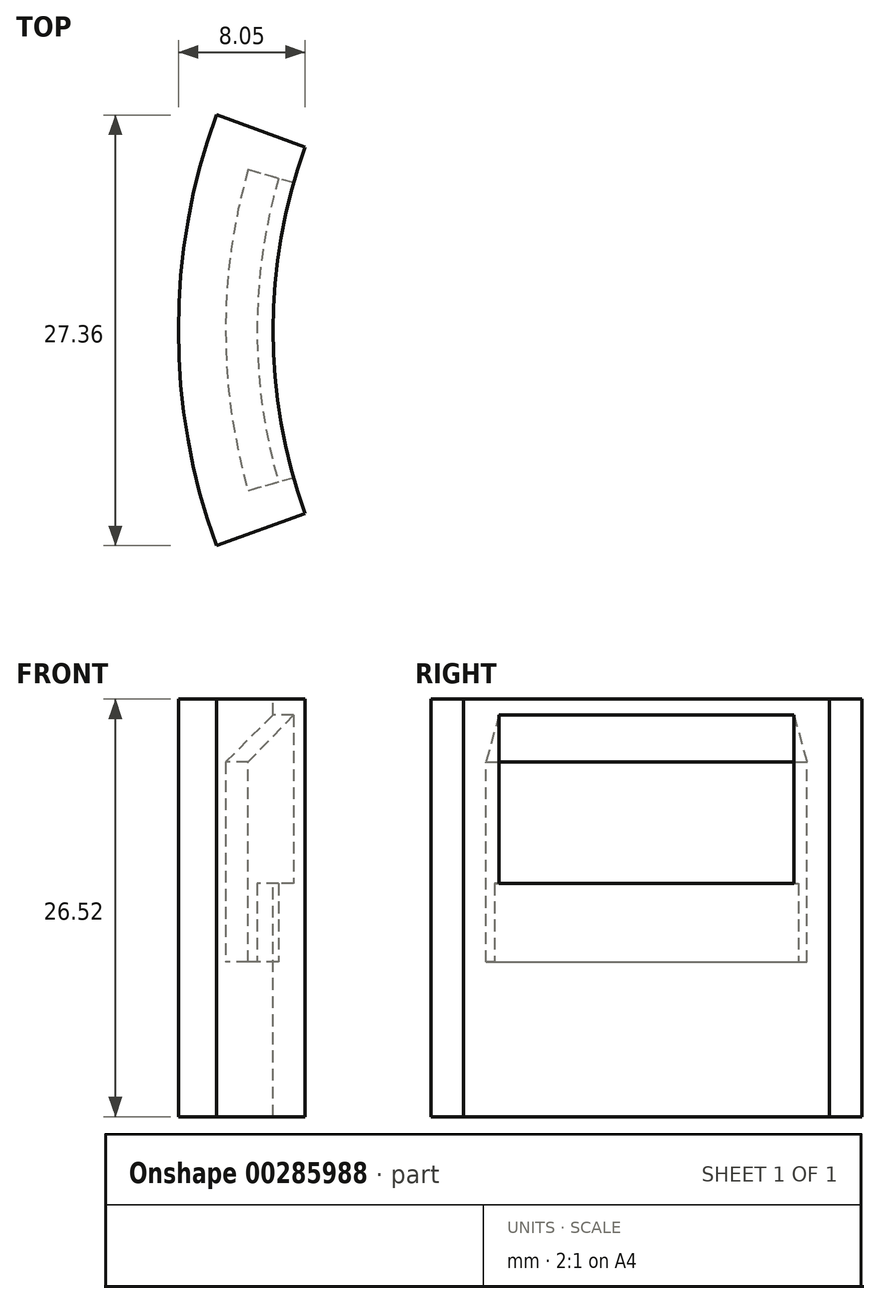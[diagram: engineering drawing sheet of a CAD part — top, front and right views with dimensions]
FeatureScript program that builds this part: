
annotation { "Feature Type Name" : "Feature", "Feature Type Description" : "" }
export const myFeature = defineFeature(function(context is Context, id is Id, definition is map)
    precondition{}
    {
        {
            var Q0;
            Q0=qCreatedBy(makeId("Front.planeOp"),FACE);
            var sketch = newSketch(context, id + "F0", { "sketchPlane" : qUnion([Q0])});
            skLineSegment(sketch, "E0", {"start": v(-34, 25.02) * mm, "end": v(0, 25.02) * mm, "construction": true});
            skLineSegment(sketch, "E1", {"start": v(-34, 25.02) * mm, "end": v(-34, 20.52) * mm});
            skLineSegment(sketch, "E2", {"start": v(-34, 20.52) * mm, "end": v(0, 20.52) * mm, "construction": true});
            skPoint(sketch, "E3", {"position": v(-34, 15.54) * mm});
            skLineSegment(sketch, "E4", {"start": v(-34, 20.52) * mm, "end": v(-37, 20.52) * mm, "construction": true});
            skLineSegment(sketch, "E5", {"start": v(-37, 20.52) * mm, "end": v(-37, 9.82) * mm});
            skPoint(sketch, "E6", {"position": v(-37, 15.17) * mm});
            skLineSegment(sketch, "E7", {"start": v(-37, 26.52) * mm, "end": v(-34, 26.52) * mm, "construction": true});
            skLineSegment(sketch, "E8", {"start": v(-34, 26.52) * mm, "end": v(-34, 25.02) * mm});
            skLineSegment(sketch, "E9", {"start": v(-34, 15.54) * mm, "end": v(-35, 15.54) * mm, "construction": true});
            skLineSegment(sketch, "E10", {"start": v(-35, 13.82) * mm, "end": v(-35, 15.54) * mm, "construction": true});
            skLineSegment(sketch, "E11", {"start": v(-34, 14.82) * mm, "end": v(-35, 14.82) * mm});
            skLineSegment(sketch, "E12", {"start": v(-35, 13.82) * mm, "end": v(-35, 14.82) * mm});
            skLineSegment(sketch, "E13", {"start": v(-35, 13.82) * mm, "end": v(-35, 9.82) * mm});
            skLineSegment(sketch, "E14", {"start": v(-35, 9.82) * mm, "end": v(-37, 9.82) * mm});
            skLineSegment(sketch, "E15", {"start": v(-37, 26.52) * mm, "end": v(-37, 23.52) * mm, "construction": true});
            skLineSegment(sketch, "E16", {"start": v(-34, 14.82) * mm, "end": v(-34, 15.54) * mm, "construction": true});
            skLineSegment(sketch, "E17", {"start": v(-34, 0) * mm, "end": v(-34, 14.82) * mm});
            skLineSegment(sketch, "E18", {"start": v(-37, 20.52) * mm, "end": v(-37, 23.52) * mm});
            skLineSegment(sketch, "E19", {"start": v(-40, 0) * mm, "end": v(-40, 26.52) * mm});
            skLineSegment(sketch, "E20", {"start": v(-34, 9.82) * mm, "end": v(-34, 8.82) * mm});
            skLineSegment(sketch, "E21", {"start": v(-34, 14.82) * mm, "end": v(-34, 20.52) * mm});
            skLineSegment(sketch, "E22", {"start": v(-34, 26.52) * mm, "end": v(-34, 25.52) * mm});
            skLineSegment(sketch, "E23", {"start": v(-34, 25.52) * mm, "end": v(-37, 22.52) * mm});
            skLineSegment(sketch, "E24", {"start": v(-34, 25.52) * mm, "end": v(-37, 25.52) * mm});
            skLineSegment(sketch, "E25", {"start": v(-40, 26.52) * mm, "end": v(-34, 26.52) * mm});
            skLineSegment(sketch, "E26", {"start": v(-34, 0) * mm, "end": v(-40, 0) * mm});
            skLineSegment(sketch, "E27", {"start": v(0, 25.02) * mm, "end": v(0, 20.52) * mm, "construction": true});
            skSolve(sketch);
        }
        {
            var Q0;
            {var subQ2=sQuery(id+"F0.wireOp",EDGE,"E5");Q0=makeQuery(id+"F0.imprint","IMPRINT",FACE,{"disambiguationData":[TD([[makeQuery(id+"F0.imprint","IMPRINT",EDGE,{"derivedFrom":subQ2}),-1.0]])]});}
            var Q1;
            Q1=makeQuery(id+"F0.imprint","IMPRINT",FACE,{"disambiguationData":[TD([[makeQuery(id+"F0.imprint","IMPRINT",EDGE,{"derivedFrom":sQuery(id+"F0.wireOp",EDGE,"E1")}),-1.0]])]});
            var Q2;
            Q2=sQuery(id+"F0.wireOp",EDGE,"E27");
            revolve(context, id + "F1", {"entities" : qUnion([Q0, Q1]), "axis" : qUnion([Q2]), "revolveType" : RevolveType.SYMMETRIC, "angle" : 40 * degree});
        }
        {
            var Q0;
            Q0=makeQuery(id+"F0.imprint","IMPRINT",FACE,{"disambiguationData":[TD([[makeQuery(id+"F0.imprint","IMPRINT",EDGE,{"derivedFrom":sQuery(id+"F0.wireOp",EDGE,"E1")}),-1.0]])]});
            var Q1;
            Q1=sQuery(id+"F0.wireOp",EDGE,"E27");
            revolve(context, id + "F2", {"operationType" : NewBodyOperationType.REMOVE, "entities" : qUnion([Q0]), "axis" : qUnion([Q1]), "revolveType" : RevolveType.SYMMETRIC, "oppositeDirection" : true, "angle" : 32 * degree});
        }
    });
